# Revit family: Towel_Bar-Delta-Vero
name_source: partatom
category: Furniture
revit_build: Autodesk Revit MEP 2012 (Build: 20110916_2132(x64)
units: mm (PartAtom-declared; Revit-internal decimal feet)

## types (4) — shared parameters
Date Modified = July 17, 2015
Default Elevation = 48 "
Description = See Part Description
Equipment Abbreviation = TB
Family Version = 1.0
Height = 1.813 "
Manufacturer = Delta Faucet Company
Model = See Part Number
Model Disclaimer = Contact Delta Faucet Company for More Information
Product Documentation Link = http://www.deltafaucet.com
Product Page URL = http://www.deltafaucet.com
URL = http://www.deltafaucet.com
z Height = 1.813 "
zero-valued in all types: z Elevation

## per-type parameters (varying)
| type | Product Material | z Type Material |
| Chrome | Chrome - Delta - Polished | 1 |
| Champagne Bronze | Bronze - Delta - Champagne | 2 |
| Venetian Bronze | Bronze - Delta - Venetian | 3 |
| Stainless | Stainless Steel - Delta - Polished | 4 |

## geometry (parser evidence)
native form markers: Blend x8, Sweep x3
no freeform markers — native parametric forms only
